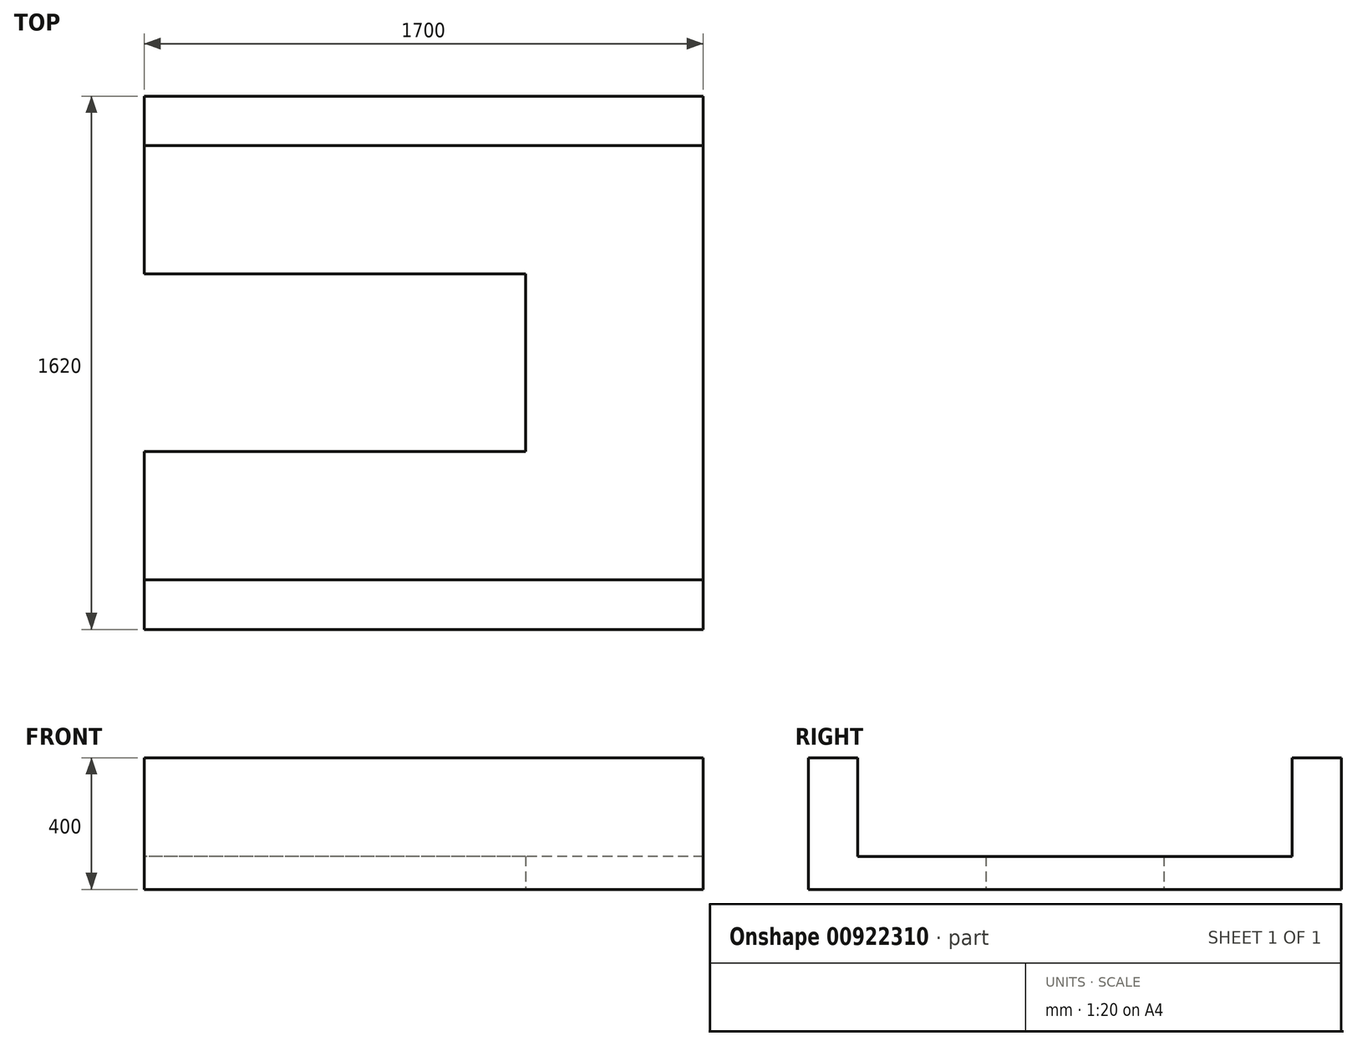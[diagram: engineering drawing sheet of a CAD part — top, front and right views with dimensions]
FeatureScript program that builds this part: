
annotation { "Feature Type Name" : "Feature", "Feature Type Description" : "" }
export const myFeature = defineFeature(function(context is Context, id is Id, definition is map)
    precondition{}
    {
        {
            var Q0;
            Q0=qCreatedBy(makeId("Top.planeOp"),FACE);
            var sketch = newSketch(context, id + "F0", { "sketchPlane" : qUnion([Q0])});
            skLineSegment(sketch, "E0", {"start": v(0, 0) * mm, "end": v(-1700, 0) * mm});
            skLineSegment(sketch, "E1", {"start": v(-1700, 0) * mm, "end": v(-1700, 540) * mm});
            skLineSegment(sketch, "E2", {"start": v(-1700, 540) * mm, "end": v(0, 540) * mm});
            skLineSegment(sketch, "E3", {"start": v(0, 540) * mm, "end": v(0, 0) * mm});
            skLineSegment(sketch, "E4", {"start": v(0, 0) * mm, "end": v(0, 150) * mm});
            skLineSegment(sketch, "E5", {"start": v(0, 150) * mm, "end": v(-1700, 150) * mm});
            skLineSegment(sketch, "E6", {"start": v(-1700, 150) * mm, "end": v(-1700, 0) * mm});
            skLineSegment(sketch, "E7", {"start": v(0, 540) * mm, "end": v(0, 1080) * mm});
            skLineSegment(sketch, "E8", {"start": v(0, 1080) * mm, "end": v(-540, 1080) * mm});
            skLineSegment(sketch, "E9", {"start": v(-540, 1080) * mm, "end": v(-540, 540) * mm});
            skLineSegment(sketch, "E10", {"start": v(-540, 540) * mm, "end": v(0, 540) * mm});
            skLineSegment(sketch, "E11", {"start": v(0, 1080) * mm, "end": v(-1700, 1080) * mm});
            skLineSegment(sketch, "E12", {"start": v(-1700, 1080) * mm, "end": v(-1700, 1620) * mm});
            skLineSegment(sketch, "E13", {"start": v(-1700, 1620) * mm, "end": v(0, 1620) * mm});
            skLineSegment(sketch, "E14", {"start": v(0, 1620) * mm, "end": v(0, 1080) * mm});
            skLineSegment(sketch, "E15", {"start": v(0, 1620) * mm, "end": v(0, 1470) * mm});
            skLineSegment(sketch, "E16", {"start": v(0, 1470) * mm, "end": v(-1700, 1470) * mm});
            skLineSegment(sketch, "E17", {"start": v(-1700, 1470) * mm, "end": v(-1700, 1620) * mm});
            skSolve(sketch);
        }
        {
            var Q0;
            {var subQ3=sQuery(id+"F0.wireOp",EDGE,"E5");Q0=makeQuery(id+"F0.imprint","IMPRINT",FACE,{"disambiguationData":[TD([[makeQuery(id+"F0.imprint","IMPRINT",EDGE,{"derivedFrom":subQ3}),-1.0]])]});}
            var Q1;
            {var subQ0=sQuery(id+"F0.wireOp",EDGE,"E7");Q1=makeQuery(id+"F0.imprint","IMPRINT",FACE,{"disambiguationData":[TD([[makeQuery(id+"F0.imprint","IMPRINT",EDGE,{"derivedFrom":subQ0}),1.0]])]});}
            var Q2;
            {var subQ1=sQuery(id+"F0.wireOp",EDGE,"E8");Q2=makeQuery(id+"F0.imprint","IMPRINT",FACE,{"disambiguationData":[TD([[makeQuery(id+"F0.imprint","IMPRINT",EDGE,{"derivedFrom":subQ1}),-1.0]])]});}
            extrude(context, id + "F1", {"entities" : qUnion([Q0, Q1, Q2]), "depth" : 100 * mm, "offsetDistance" : 25 * mm});
        }
        {
            var Q0;
            {var subQ0=sQuery(id+"F0.wireOp",EDGE,"E0");Q0=makeQuery(id+"F0.imprint","IMPRINT",FACE,{"disambiguationData":[TD([[makeQuery(id+"F0.imprint","IMPRINT",EDGE,{"derivedFrom":subQ0}),-1.0]])]});}
            var Q1;
            {var subQ0=sQuery(id+"F0.wireOp",EDGE,"E13");Q1=makeQuery(id+"F0.imprint","IMPRINT",FACE,{"disambiguationData":[TD([[makeQuery(id+"F0.imprint","IMPRINT",EDGE,{"derivedFrom":subQ0}),-1.0]])]});}
            extrude(context, id + "F2", {"entities" : qUnion([Q0, Q1]), "operationType" : NewBodyOperationType.ADD, "depth" : 400 * mm, "offsetDistance" : 25 * mm});
        }
    });
